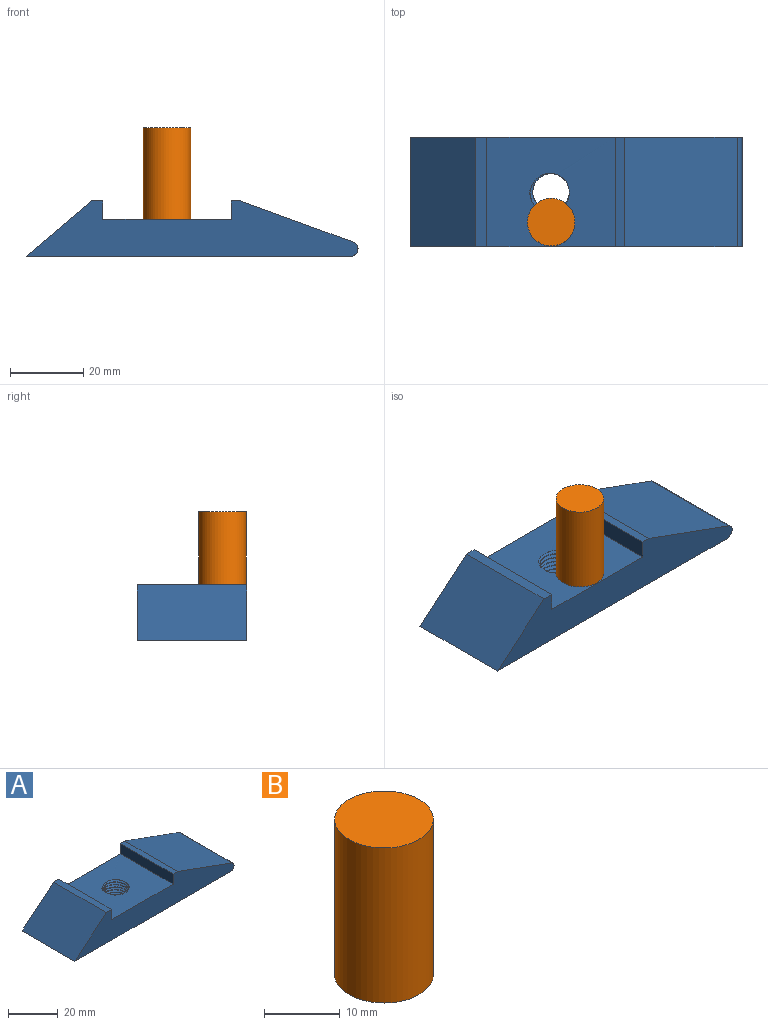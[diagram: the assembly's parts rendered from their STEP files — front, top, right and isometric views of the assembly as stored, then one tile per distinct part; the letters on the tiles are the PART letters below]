
ASSEMBLY  parts=2 mates=1
PART A: 15 faces, bbox 91.2x30.6x15.7 mm
  f0: cylinder r=5mm len=10.1mm, axis (0,0,1), area 38.7mm2, adj f3,f11,f12,f13,f14
  f1: plane 30x3.02mm, normal (0,0,1), area 90.7mm2, adj f2,f6,f7,f9
  f2: plane 90.66x15.1mm, normal (0,-1,0), area 868.8mm2, adj f1,f3,f4,f5,f6,f8,f9,f10
  f3: plane 88.66x30mm, normal (0,0,-1), area 2581.2mm2, adj f0,f2,f6,f7,f8
  f4: plane 30.83x30mm, normal (0.34,0,0.94), area 984.2mm2, adj f2,f5,f7,f8
  f5: plane 30x2.5mm, normal (0,0,1), area 74.9mm2, adj f2,f4,f7,f10
  f6: plane 30x18mm, normal (-0.64,0,0.77), area 704.7mm2, adj f1,f2,f3,f7
  f7: plane 90.66x15.1mm, normal (0,1,0), area 868.8mm2, adj f1,f3,f4,f5,f6,f8,f9,f10
  f8: cylinder r=2mm len=30mm, axis (0,1,0), area 167.6mm2, adj f2,f3,f4,f7
  f9: plane 30x5mm, normal (1,0,0), area 150mm2, adj f1,f2,f7,f11
  f10: plane 30x5mm, normal (-1,0,0), area 150mm2, adj f2,f5,f7,f11
  f11: plane 35.58x30.58mm, normal (0,0,1), area 960.1mm2, adj f0,f2,f7,f9,f10,f13,f14
  f12: plane 1x0.87mm, normal (0,1,0.04), area 0.4mm2, adj f0,f13,f14
  f13: bspline ~13.55x11.76mm, area 252.6mm2, adj f0,f11,f12,f14
  f14: bspline ~13.55x11.76mm, area 267.3mm2, adj f0,f11,f12,f13
PART B: 3 faces, bbox 13x13x25 mm
  f0: cylinder r=6.5mm len=25mm, axis (0,0,-1), area 1021mm2, adj f1,f2
  f1: plane 13x13mm, normal (0,0,1), area 132.7mm2, adj f0
  f2: plane 13x13mm, normal (0,0,-1), area 132.7mm2, adj f0
PLACE A t=(-4.82,-10.41,5.88)mm
PLACE B t=(-24.47,-47.54,15.98)mm
MATE planar B.f0 <-> A.f11  axis (0,0,-1) through (-66.28,-33.69,15.98)mm
